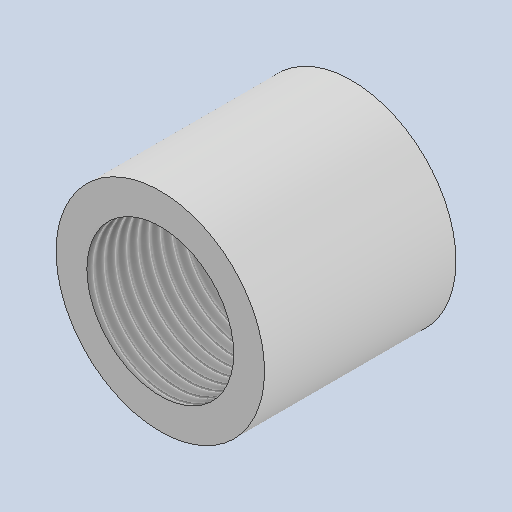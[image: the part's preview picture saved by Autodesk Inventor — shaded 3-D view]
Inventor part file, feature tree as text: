
AUTODESK INVENTOR PART (.ipt)
format: ipt  version: 2023.2 (Build 272271030, 271C)  size: 147,968 bytes
history: native  units: mm
features: sketch x2, extrude x1, hole x1
ambient origin geometry x8: Origin, YZ Plane, XZ Plane, XY Plane, X Axis, Y Axis, Z Axis, Center Point
bodies: Solid1 (feature_tree)
feature tree (4):
  extrude  "Extrusion1"  Depth=39.5mm
  hole  "Hole1"  [1 undecoded]
  sketch  "Sketch1"  dims[d2=39.5mm d3=0.0mm d4=43.0mm]
  sketch  "Sketch2"  dims[d5=30.291mm d6=66.498mm d7=4.0mm d8=2.0mm d9=90.0deg d10=76.498mm d11=20.594885mm]
note: 1 required parameter value undecoded (feature->parameter linkage not recoverable at this tier; creation-order binding heuristic only, values carry confidence <= 0.55)
